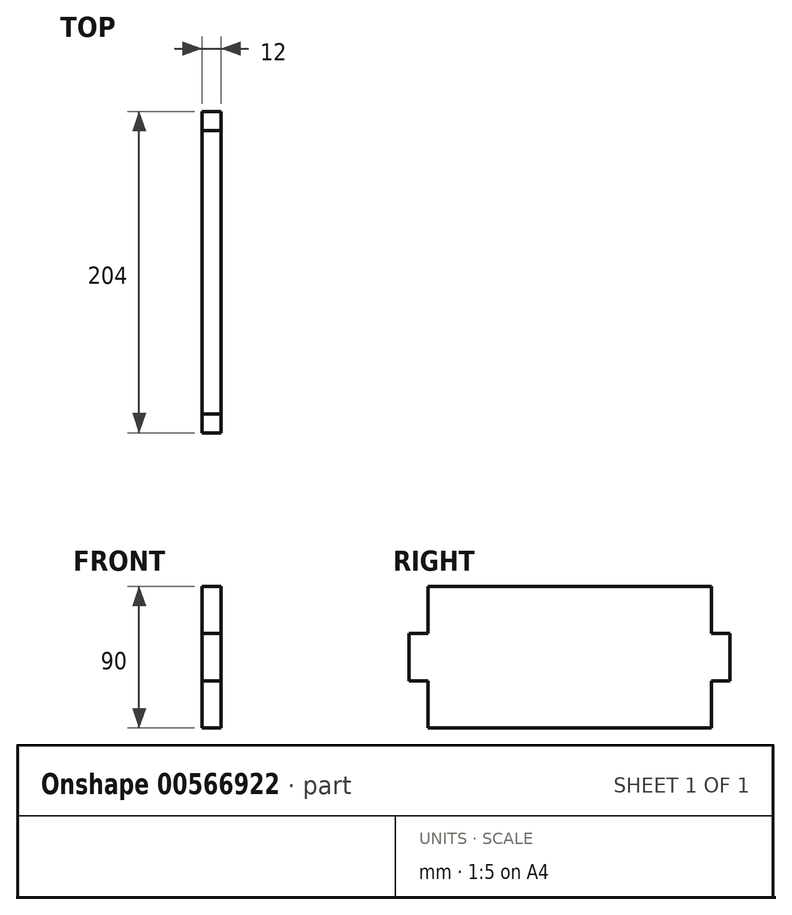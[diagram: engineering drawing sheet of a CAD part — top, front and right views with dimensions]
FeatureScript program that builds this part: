
annotation { "Feature Type Name" : "Feature", "Feature Type Description" : "" }
export const myFeature = defineFeature(function(context is Context, id is Id, definition is map)
    precondition{}
    {
        {
            var Q0;
            Q0=qCreatedBy(makeId("Right.planeOp"),FACE);
            var sketch = newSketch(context, id + "F0", { "sketchPlane" : qUnion([Q0])});
            skLineSegment(sketch, "E0", {"start": v(0, 0) * mm, "end": v(0, 30) * mm});
            skLineSegment(sketch, "E1", {"start": v(0, 30) * mm, "end": v(-12, 30) * mm});
            skLineSegment(sketch, "E2", {"start": v(-12, 30) * mm, "end": v(-12, 60) * mm});
            skLineSegment(sketch, "E3", {"start": v(-12, 60) * mm, "end": v(0, 60) * mm});
            skLineSegment(sketch, "E4", {"start": v(0, 60) * mm, "end": v(0, 90) * mm});
            skLineSegment(sketch, "E5", {"start": v(0, 0) * mm, "end": v(90, 0) * mm});
            skLineSegment(sketch, "E6", {"start": v(0, 90) * mm, "end": v(90, 90) * mm});
            skLineSegment(sketch, "E7", {"start": v(90, 90) * mm, "end": v(90, 0) * mm});
            skLineSegment(sketch, "E8.MirrorCS", {"start": v(192, 60) * mm, "end": v(180, 60) * mm});
            skLineSegment(sketch, "E9.MirrorCS", {"start": v(180, 30) * mm, "end": v(192, 30) * mm});
            skLineSegment(sketch, "E10.MirrorCS", {"start": v(180, 0) * mm, "end": v(180, 30) * mm});
            skLineSegment(sketch, "E11.MirrorCS", {"start": v(192, 30) * mm, "end": v(192, 60) * mm});
            skLineSegment(sketch, "E12.MirrorCS", {"start": v(180, 60) * mm, "end": v(180, 90) * mm});
            skLineSegment(sketch, "E13.MirrorCS", {"start": v(180, 0) * mm, "end": v(90, 0) * mm});
            skLineSegment(sketch, "E14.MirrorCS", {"start": v(180, 90) * mm, "end": v(90, 90) * mm});
            skSolve(sketch);
        }
        {
            var Q0;
            Q0 = qSketchRegion(id + "F0", true);
            extrude(context, id + "F1", {"entities" : qUnion([Q0]), "depth" : 12 * mm, "offsetDistance" : 25 * mm});
        }
    });
